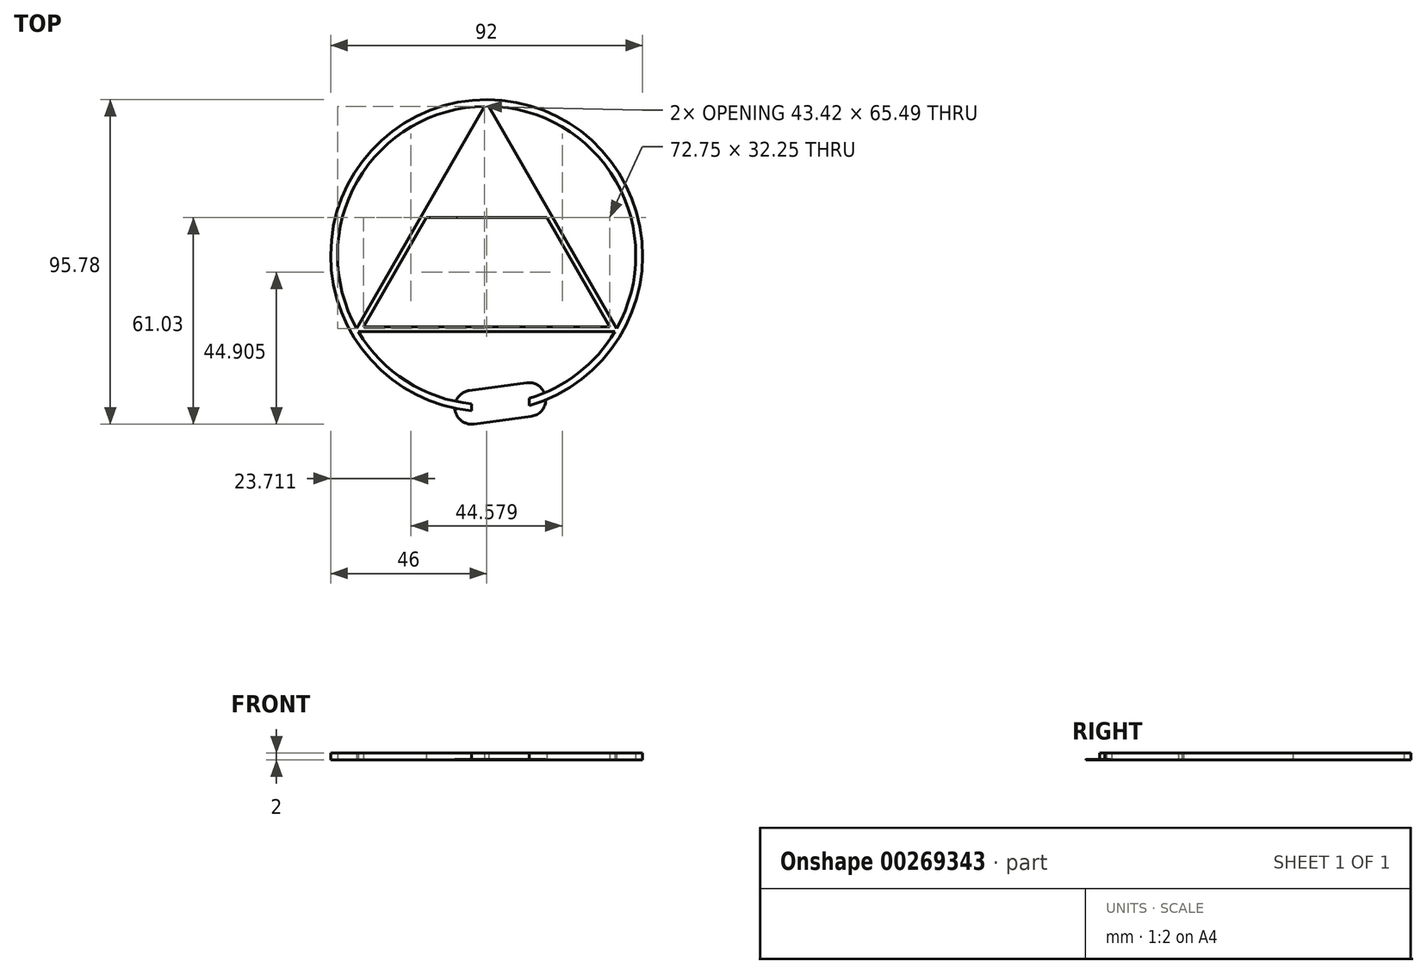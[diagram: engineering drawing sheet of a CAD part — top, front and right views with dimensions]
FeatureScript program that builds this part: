
annotation { "Feature Type Name" : "Feature", "Feature Type Description" : "" }
export const myFeature = defineFeature(function(context is Context, id is Id, definition is map)
    precondition{}
    {
        {
            var Q0;
            Q0=qCreatedBy(makeId("Top.planeOp"),FACE);
            var sketch = newSketch(context, id + "F0", { "sketchPlane" : qUnion([Q0])});
            skCircle(sketch, "E0", {"center": v(0, 0) * mm, "radius": 45 * mm});
            skCircle(sketch, "E1.cCircle", {"center": v(0, 0) * mm, "radius": 45 * mm, "construction": true});
            skLineSegment(sketch, "E1.0", {"start": v(0, 45) * mm, "end": v(38.97, -22.5) * mm});
            skLineSegment(sketch, "E1.1", {"start": v(38.97, -22.5) * mm, "end": v(-38.97, -22.5) * mm});
            skLineSegment(sketch, "E1.2", {"start": v(-38.97, -22.5) * mm, "end": v(0, 45) * mm});
            skCircle(sketch, "E2.0", {"center": v(0, 0) * mm, "radius": 46 * mm});
            skCircle(sketch, "E3.0", {"center": v(0, 0) * mm, "radius": 44 * mm});
            skLineSegment(sketch, "E4.0", {"start": v(-36.37, -21) * mm, "end": v(0, 42) * mm});
            skLineSegment(sketch, "E4.1", {"start": v(36.37, -21) * mm, "end": v(-36.37, -21) * mm});
            skLineSegment(sketch, "E4.2", {"start": v(0, 42) * mm, "end": v(36.37, -21) * mm});
            skLineSegment(sketch, "E5", {"start": v(-19.49, 11.25) * mm, "end": v(19.49, 11.25) * mm});
            skSolve(sketch);
        }
        {
            var Q0;
            Q0=makeQuery(id+"F0.imprint","IMPRINT",FACE,{"disambiguationData":[TD([[makeQuery(id+"F0.imprint","IMPRINT",EDGE,{"derivedFrom":sQuery(id+"F0.wireOp",EDGE,"E2.0")}),1.0]])]});
            var Q1;
            {var subQ0=sQuery(id+"F0.wireOp",EDGE,"E1.2");var subQ4=sQuery(id+"F0.wireOp",EDGE,"E3.0");var subQ5=makeQuery(id+"F0.imprint","INTERSECT",VERTEX,{"disambiguationData":[OD(0.0)],"derivedFrom":[subQ0,subQ4]});Q1=makeQuery(id+"F0.imprint","IMPRINT",FACE,{"disambiguationData":[TD([[makeQuery(id+"F0.imprint","IMPRINT",EDGE,{"disambiguationData":[TD([[subQ5,1.0]])],"derivedFrom":subQ4}),-1.0]])]});}
            var Q2;
            Q2=makeQuery(id+"F0.imprint","IMPRINT",FACE,{"disambiguationData":[TD([[makeQuery(id+"F0.imprint","IMPRINT",EDGE,{"derivedFrom":sQuery(id+"F0.wireOp",EDGE,"E4.0")}),1.0]])]});
            var Q3;
            {var subQ0=sQuery(id+"F0.wireOp",EDGE,"E1.0");var subQ4=sQuery(id+"F0.wireOp",EDGE,"E3.0");var subQ5=makeQuery(id+"F0.imprint","INTERSECT",VERTEX,{"disambiguationData":[OD(0.0)],"derivedFrom":[subQ0,subQ4]});Q3=makeQuery(id+"F0.imprint","IMPRINT",FACE,{"disambiguationData":[TD([[makeQuery(id+"F0.imprint","IMPRINT",EDGE,{"disambiguationData":[TD([[subQ5,1.0]])],"derivedFrom":subQ4}),-1.0]])]});}
            var Q4;
            {var subQ0=sQuery(id+"F0.wireOp",EDGE,"E1.1");var subQ4=sQuery(id+"F0.wireOp",EDGE,"E3.0");var subQ5=makeQuery(id+"F0.imprint","INTERSECT",VERTEX,{"disambiguationData":[OD(0.0)],"derivedFrom":[subQ0,subQ4]});Q4=makeQuery(id+"F0.imprint","IMPRINT",FACE,{"disambiguationData":[TD([[makeQuery(id+"F0.imprint","IMPRINT",EDGE,{"disambiguationData":[TD([[subQ5,1.0]])],"derivedFrom":subQ4}),-1.0]])]});}
            var Q5;
            {var subQ1=sQuery(id+"F0.wireOp",EDGE,"E1.0");var subQ3=sQuery(id+"F0.wireOp",EDGE,"E3.0");var subQ4=makeQuery(id+"F0.imprint","INTERSECT",VERTEX,{"disambiguationData":[OD(1.0)],"derivedFrom":[subQ1,subQ3]});Q5=makeQuery(id+"F0.imprint","IMPRINT",FACE,{"disambiguationData":[TD([[makeQuery(id+"F0.imprint","IMPRINT",EDGE,{"disambiguationData":[TD([[subQ4,1.0]])],"derivedFrom":subQ3}),-1.0]])]});}
            var Q6;
            {var subQ1=sQuery(id+"F0.wireOp",EDGE,"E1.0");var subQ3=sQuery(id+"F0.wireOp",EDGE,"E3.0");var subQ4=makeQuery(id+"F0.imprint","INTERSECT",VERTEX,{"disambiguationData":[OD(0.0)],"derivedFrom":[subQ1,subQ3]});Q6=makeQuery(id+"F0.imprint","IMPRINT",FACE,{"disambiguationData":[TD([[makeQuery(id+"F0.imprint","IMPRINT",EDGE,{"disambiguationData":[TD([[subQ4,-1.0]])],"derivedFrom":subQ3}),-1.0]])]});}
            var Q7;
            {var subQ1=sQuery(id+"F0.wireOp",EDGE,"E1.1");var subQ3=sQuery(id+"F0.wireOp",EDGE,"E3.0");var subQ4=makeQuery(id+"F0.imprint","INTERSECT",VERTEX,{"disambiguationData":[OD(1.0)],"derivedFrom":[subQ1,subQ3]});Q7=makeQuery(id+"F0.imprint","IMPRINT",FACE,{"disambiguationData":[TD([[makeQuery(id+"F0.imprint","IMPRINT",EDGE,{"disambiguationData":[TD([[subQ4,1.0]])],"derivedFrom":subQ3}),-1.0]])]});}
            var Q8;
            {var subQ8=sQuery(id+"F0.wireOp",EDGE,"E4.1");Q8=makeQuery(id+"F0.imprint","IMPRINT",FACE,{"disambiguationData":[TD([[makeQuery(id+"F0.imprint","IMPRINT",EDGE,{"derivedFrom":subQ8}),1.0]])]});}
            var Q9;
            {var subQ0=sQuery(id+"F0.wireOp",EDGE,"E4.2");var subQ1=sQuery(id+"F0.wireOp",EDGE,"E4.0");var subQ2=makeQuery(id+"F0.imprint","INTERSECT",VERTEX,{"derivedFrom":[subQ1,subQ0]});Q9=makeQuery(id+"F0.imprint","IMPRINT",FACE,{"disambiguationData":[TD([[makeQuery(id+"F0.imprint","IMPRINT",EDGE,{"disambiguationData":[TD([[subQ2,1.0]])],"derivedFrom":subQ1}),-1.0]])]});}
            extrude(context, id + "F1", {"entities" : qUnion([Q0, Q1, Q2, Q3, Q4, Q5, Q6, Q7, Q8, Q9]), "endBound" : BoundingType.SYMMETRIC, "depth" : 2 * mm});
        }
        {
            var Q0;
            Q0=qCreatedBy(makeId("Top.planeOp"),FACE);
            var sketch = newSketch(context, id + "F2", { "sketchPlane" : qUnion([Q0])});
            skLineSegment(sketch, "E6.bottom", {"start": v(12.6, 0) * mm, "end": v(-4.4, 0) * mm});
            skLineSegment(sketch, "E6.top", {"start": v(12.6, -58.26) * mm, "end": v(-4.4, -58.26) * mm});
            skLineSegment(sketch, "E6.left", {"start": v(12.6, 0) * mm, "end": v(12.6, -58.26) * mm});
            skLineSegment(sketch, "E6.right", {"start": v(-4.4, 0) * mm, "end": v(-4.4, -58.26) * mm});
            skLineSegment(sketch, "E7", {"start": v(12.6, -35.24) * mm, "end": v(-4.4, -35.24) * mm});
            skSolve(sketch);
        }
        {
            var Q0;
            {var subQ0=sQuery(id+"F2.wireOp",EDGE,"E6.top");Q0=makeQuery(id+"F2.imprint","IMPRINT",FACE,{"disambiguationData":[TD([[makeQuery(id+"F2.imprint","IMPRINT",EDGE,{"derivedFrom":subQ0}),-1.0]])]});}
            extrude(context, id + "F3", {"entities" : qUnion([Q0]), "operationType" : NewBodyOperationType.REMOVE, "endBound" : BoundingType.SYMMETRIC, "oppositeDirection" : true, "depth" : 25 * mm});
        }
        {
            var Q0;
            Q0=qCreatedBy(makeId("Top.planeOp"),FACE);
            var sketch = newSketch(context, id + "F4", { "sketchPlane" : qUnion([Q0])});
            skCircle(sketch, "E8", {"center": v(-4.4, -44.78) * mm, "radius": 5 * mm});
            skCircle(sketch, "E9", {"center": v(12.45, -42.51) * mm, "radius": 5 * mm});
            skLineSegment(sketch, "E10", {"start": v(-3.73, -49.74) * mm, "end": v(13.12, -47.47) * mm});
            skLineSegment(sketch, "E11", {"start": v(-5.07, -39.83) * mm, "end": v(11.78, -37.56) * mm});
            skSolve(sketch);
        }
        {
            var Q0;
            Q0 = qSketchRegion(id + "F4", true);
            var Q1;
            Q1=makeQuery(id+"F1.opExtrude","CAP_FACE",FACE,{"disambiguationData":[OSD([sQuery(id+"F0.wireOp",EDGE,"E1.0"),sQuery(id+"F0.wireOp",EDGE,"E1.1"),sQuery(id+"F0.wireOp",EDGE,"E1.2"),sQuery(id+"F0.wireOp",EDGE,"E2.0"),sQuery(id+"F0.wireOp",EDGE,"E3.0"),sQuery(id+"F0.wireOp",EDGE,"E4.0"),sQuery(id+"F0.wireOp",EDGE,"E4.1"),sQuery(id+"F0.wireOp",EDGE,"E4.2"),sQuery(id+"F0.wireOp",EDGE,"E5")])],"isStart":true});
            extrude(context, id + "F5", {"entities" : qUnion([Q0]), "operationType" : NewBodyOperationType.ADD, "endBound" : BoundingType.UP_TO_SURFACE, "oppositeDirection" : true, "endBoundEntityFace" : qUnion([Q1]), "depth" : 25 * mm, "hasSecondDirection" : true, "secondDirectionOppositeDirection" : true, "secondDirectionDepth" : 0.9 * mm});
        }
    });
